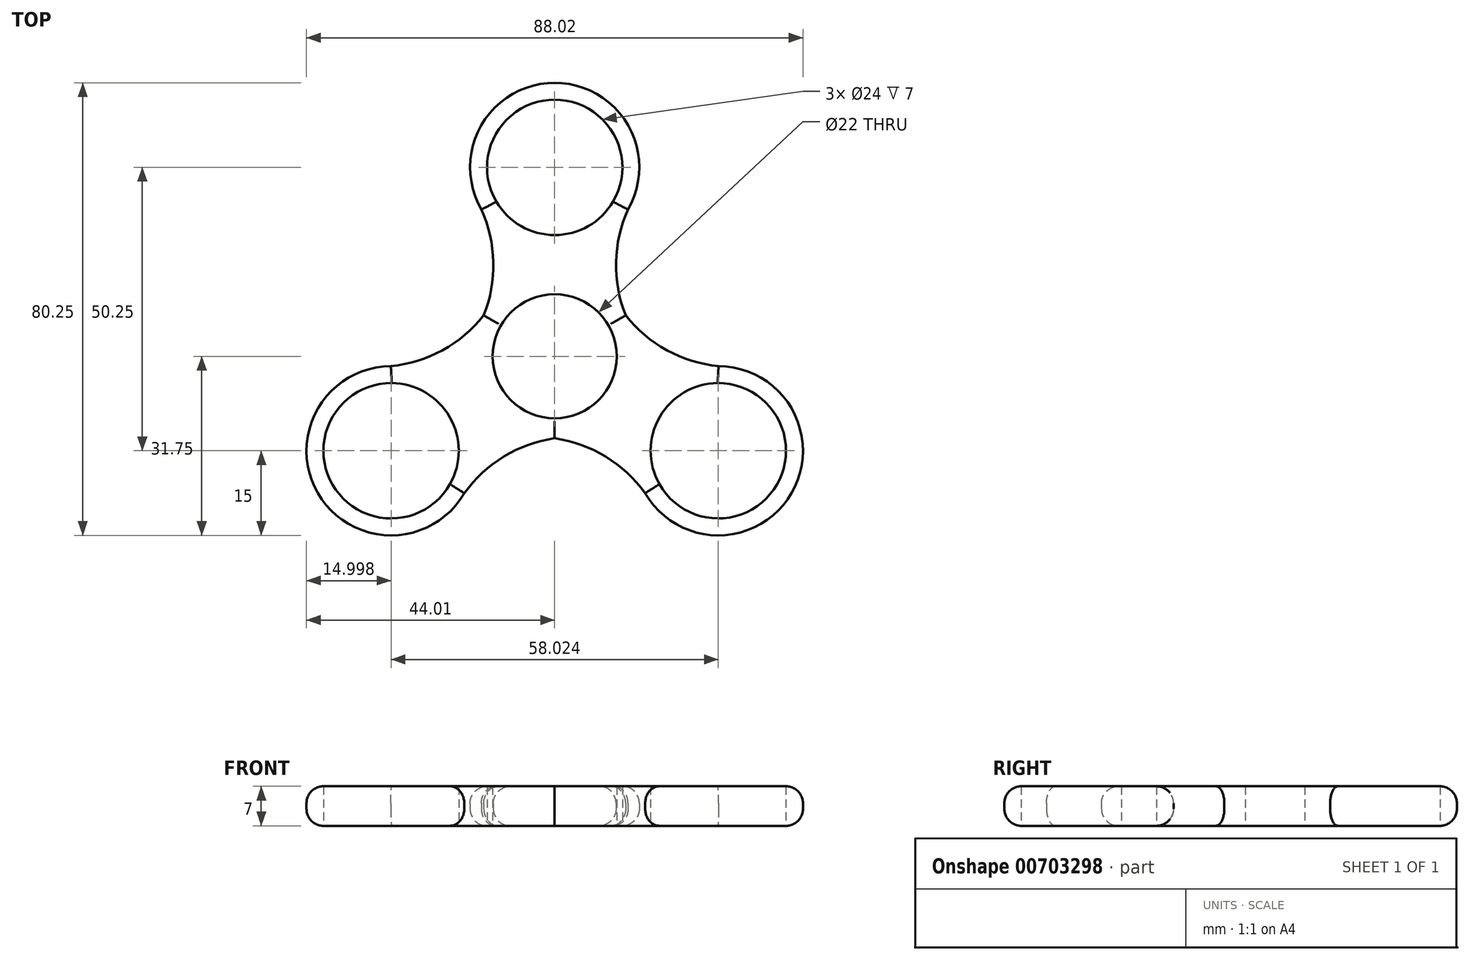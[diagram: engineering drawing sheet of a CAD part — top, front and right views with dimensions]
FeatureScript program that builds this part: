
annotation { "Feature Type Name" : "Feature", "Feature Type Description" : "" }
export const myFeature = defineFeature(function(context is Context, id is Id, definition is map)
    precondition{}
    {
        {
            var Q0;
            Q0=qCreatedBy(makeId("Top.planeOp"),FACE);
            var sketch = newSketch(context, id + "F0", { "sketchPlane" : qUnion([Q0])});
            skCircle(sketch, "E0", {"center": v(0, 0) * mm, "radius": 11 * mm});
            skCircle(sketch, "E1", {"center": v(0, 0) * mm, "radius": 14.5 * mm});
            skCircle(sketch, "E2", {"center": v(0, 0) * mm, "radius": 48.5 * mm, "construction": true});
            skCircle(sketch, "E3", {"center": v(0, 33.5) * mm, "radius": 12 * mm});
            skCircle(sketch, "E4", {"center": v(0, 33.5) * mm, "radius": 15 * mm});
            skCircle(sketch, "E5.1.0", {"center": v(-29.01, -16.75) * mm, "radius": 15 * mm});
            skCircle(sketch, "E5.1.1", {"center": v(-29.01, -16.75) * mm, "radius": 12 * mm});
            skArc(sketch, "E5.1.3", {"start": v(0, -14.52) * mm, "mid": v(-9.01, -17.77) * mm, "end": v(-16.04, -24.28) * mm});
            skCircle(sketch, "E5.2.0", {"center": v(29.01, -16.75) * mm, "radius": 15 * mm});
            skCircle(sketch, "E5.2.1", {"center": v(29.01, -16.75) * mm, "radius": 12 * mm});
            skArc(sketch, "E5.2.2", {"start": v(0, -14.52) * mm, "mid": v(9.01, -17.77) * mm, "end": v(16.04, -24.28) * mm});
            skPoint(sketch, "E6", {"position": v(-12.58, 7.26) * mm});
            skArc(sketch, "E7.trimOffspring", {"start": v(-12.58, 7.26) * mm, "mid": v(-19.9, 1.08) * mm, "end": v(-29.05, -1.75) * mm});
            skArc(sketch, "E8.trimOffspring", {"start": v(-12.58, 7.26) * mm, "mid": v(-10.88, 16.69) * mm, "end": v(-13, 26.03) * mm});
            skPoint(sketch, "E9.start.orphan", {"position": v(-13.6, 5.04) * mm});
            skPoint(sketch, "E10", {"position": v(12.58, 7.26) * mm});
            skArc(sketch, "E11.trimOffspring", {"start": v(12.58, 7.26) * mm, "mid": v(19.9, 1.08) * mm, "end": v(29.05, -1.75) * mm});
            skArc(sketch, "E12.trimOffspring", {"start": v(12.58, 7.26) * mm, "mid": v(10.88, 16.69) * mm, "end": v(13, 26.03) * mm});
            skPoint(sketch, "E13.MirrorCS.start.orphan", {"position": v(13.6, 5.04) * mm});
            skPoint(sketch, "E14", {"position": v(0, -14.52) * mm});
            skPoint(sketch, "E15.orphan", {"position": v(-2.43, -14.3) * mm});
            skPoint(sketch, "E16.orphan", {"position": v(2.43, -14.3) * mm});
            skSolve(sketch);
        }
        {
            var Q0;
            Q0=qSketchRegion(id+"F0",true);
            var Q1;
            Q1=makeQuery(id+"F0.imprint","IMPRINT",FACE,{"disambiguationData":[TD([[makeQuery(id+"F0.imprint","IMPRINT",EDGE,{"derivedFrom":sQuery(id+"F0.wireOp",EDGE,"E0")}),-1.0]])]});
            extrude(context, id + "F1", {"entities" : qUnion([Q0, Q1]), "depth" : 7 * mm, "offsetDistance" : 25 * mm});
        }
        {
            var Q0;
            Q0=makeQuery(id+"F1.opExtrude","CAP_EDGE",EDGE,{"disambiguationData":[OSD([sQuery(id+"F0.wireOp",EDGE,"E4")])],"isStart":false});
            var Q1;
            Q1=makeQuery(id+"F1.opExtrude","CAP_EDGE",EDGE,{"disambiguationData":[OSD([sQuery(id+"F0.wireOp",EDGE,"E12.trimOffspring")])],"isStart":false});
            var Q2;
            Q2=makeQuery(id+"F1.opExtrude","CAP_EDGE",EDGE,{"disambiguationData":[OSD([sQuery(id+"F0.wireOp",EDGE,"E11.trimOffspring")])],"isStart":false});
            var Q3;
            Q3=makeQuery(id+"F1.opExtrude","CAP_EDGE",EDGE,{"disambiguationData":[OSD([sQuery(id+"F0.wireOp",EDGE,"E5.2.0")])],"isStart":false});
            var Q4;
            Q4=makeQuery(id+"F1.opExtrude","CAP_EDGE",EDGE,{"disambiguationData":[OSD([sQuery(id+"F0.wireOp",EDGE,"E5.2.2")])],"isStart":false});
            var Q5;
            Q5=makeQuery(id+"F1.opExtrude","CAP_EDGE",EDGE,{"disambiguationData":[OSD([sQuery(id+"F0.wireOp",EDGE,"E5.1.3")])],"isStart":false});
            var Q6;
            Q6=makeQuery(id+"F1.opExtrude","CAP_EDGE",EDGE,{"disambiguationData":[OSD([sQuery(id+"F0.wireOp",EDGE,"E5.1.0")])],"isStart":false});
            var Q7;
            Q7=makeQuery(id+"F1.opExtrude","CAP_EDGE",EDGE,{"disambiguationData":[OSD([sQuery(id+"F0.wireOp",EDGE,"E7.trimOffspring")])],"isStart":false});
            var Q8;
            Q8=makeQuery(id+"F1.opExtrude","CAP_EDGE",EDGE,{"disambiguationData":[OSD([sQuery(id+"F0.wireOp",EDGE,"E8.trimOffspring")])],"isStart":false});
            fillet(context, id + "F2", {"entities" : qUnion([Q0, Q1, Q2, Q3, Q4, Q5, Q6, Q7, Q8]), "radius" : 3 * mm, "tangentPropagation" : true, "allowEdgeOverflow" : false});
        }
        {
            var Q0;
            Q0=makeQuery(id+"F1.opExtrude","CAP_EDGE",EDGE,{"disambiguationData":[OSD([sQuery(id+"F0.wireOp",EDGE,"E4")])],"isStart":true});
            var Q1;
            Q1=makeQuery(id+"F1.opExtrude","CAP_EDGE",EDGE,{"disambiguationData":[OSD([sQuery(id+"F0.wireOp",EDGE,"E8.trimOffspring")])],"isStart":true});
            var Q2;
            Q2=makeQuery(id+"F1.opExtrude","CAP_EDGE",EDGE,{"disambiguationData":[OSD([sQuery(id+"F0.wireOp",EDGE,"E7.trimOffspring")])],"isStart":true});
            var Q3;
            Q3=makeQuery(id+"F1.opExtrude","CAP_EDGE",EDGE,{"disambiguationData":[OSD([sQuery(id+"F0.wireOp",EDGE,"E5.1.0")])],"isStart":true});
            var Q4;
            Q4=makeQuery(id+"F1.opExtrude","CAP_EDGE",EDGE,{"disambiguationData":[OSD([sQuery(id+"F0.wireOp",EDGE,"E5.1.3")])],"isStart":true});
            var Q5;
            Q5=makeQuery(id+"F1.opExtrude","CAP_EDGE",EDGE,{"disambiguationData":[OSD([sQuery(id+"F0.wireOp",EDGE,"E5.2.2")])],"isStart":true});
            var Q6;
            Q6=makeQuery(id+"F1.opExtrude","CAP_EDGE",EDGE,{"disambiguationData":[OSD([sQuery(id+"F0.wireOp",EDGE,"E5.2.0")])],"isStart":true});
            var Q7;
            Q7=makeQuery(id+"F1.opExtrude","CAP_EDGE",EDGE,{"disambiguationData":[OSD([sQuery(id+"F0.wireOp",EDGE,"E11.trimOffspring")])],"isStart":true});
            var Q8;
            Q8=makeQuery(id+"F1.opExtrude","CAP_EDGE",EDGE,{"disambiguationData":[OSD([sQuery(id+"F0.wireOp",EDGE,"E12.trimOffspring")])],"isStart":true});
            fillet(context, id + "F3", {"entities" : qUnion([Q0, Q1, Q2, Q3, Q4, Q5, Q6, Q7, Q8]), "radius" : 3 * mm, "tangentPropagation" : true, "allowEdgeOverflow" : false});
        }
    });
